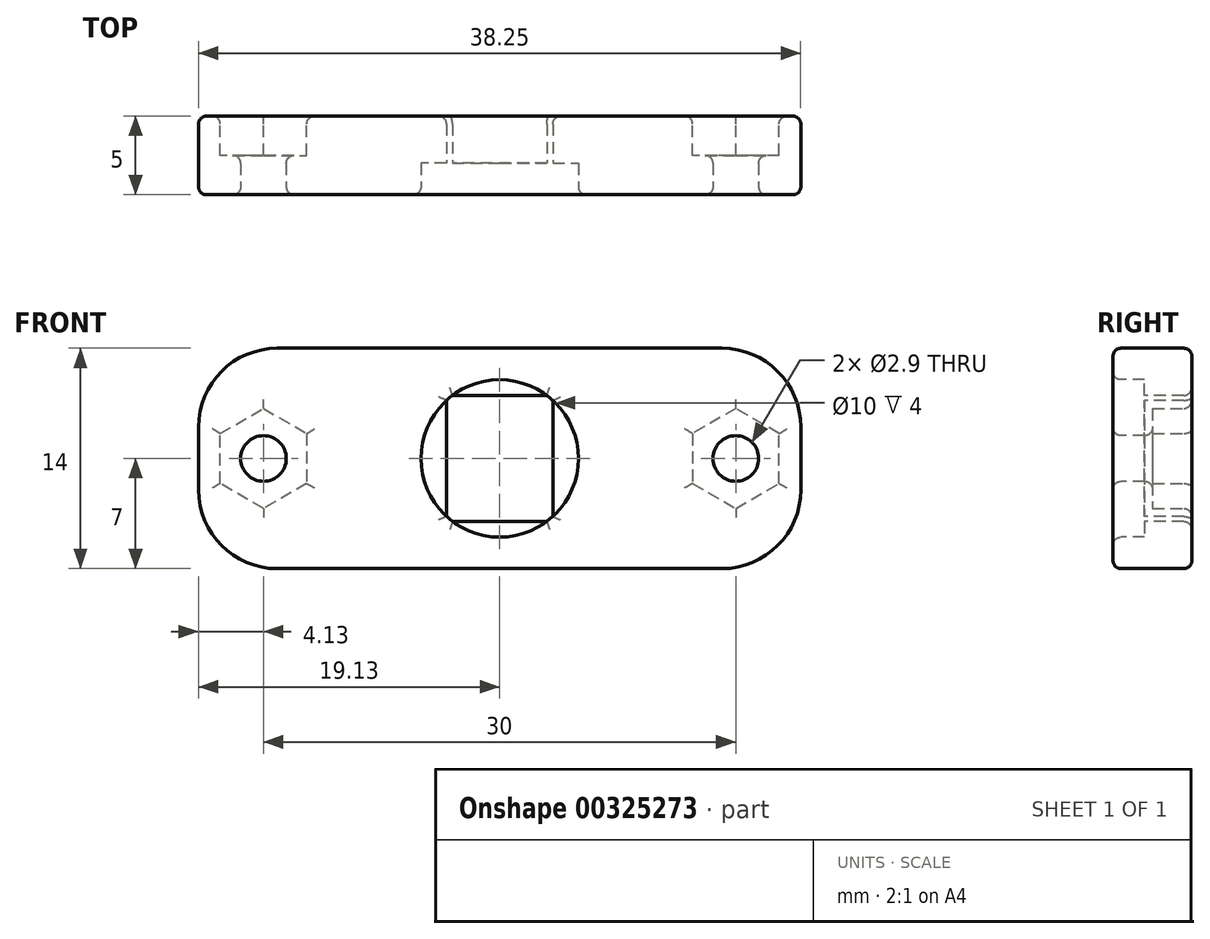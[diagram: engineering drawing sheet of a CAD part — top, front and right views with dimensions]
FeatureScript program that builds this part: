
annotation { "Feature Type Name" : "Feature", "Feature Type Description" : "" }
export const myFeature = defineFeature(function(context is Context, id is Id, definition is map)
    precondition{}
    {
        {
            var Q0;
            Q0=qCreatedBy(makeId("Front.planeOp"),FACE);
            var sketch = newSketch(context, id + "F0", { "sketchPlane" : qUnion([Q0])});
            skLineSegment(sketch, "E0.bottom", {"start": v(14.12, 7) * mm, "end": v(-14.12, 7) * mm});
            skLineSegment(sketch, "E0.top", {"start": v(14.13, -7) * mm, "end": v(-14.12, -7) * mm});
            skLineSegment(sketch, "E0.left", {"start": v(19.13, 2) * mm, "end": v(19.13, -2) * mm});
            skLineSegment(sketch, "E0.right", {"start": v(-19.12, 2) * mm, "end": v(-19.12, -2) * mm});
            skPoint(sketch, "E1.visualSharp", {"position": v(19.13, 7) * mm});
            skArc(sketch, "E1.filletArc", {"start": v(19.13, 2) * mm, "mid": v(17.66, 5.54) * mm, "end": v(14.12, 7) * mm});
            skPoint(sketch, "E2.visualSharp", {"position": v(19.13, -7) * mm});
            skArc(sketch, "E2.filletArc", {"start": v(14.13, -7) * mm, "mid": v(17.66, -5.54) * mm, "end": v(19.13, -2) * mm});
            skPoint(sketch, "E3.visualSharp", {"position": v(-19.12, -7) * mm});
            skArc(sketch, "E3.filletArc", {"start": v(-19.12, -2) * mm, "mid": v(-17.66, -5.54) * mm, "end": v(-14.12, -7) * mm});
            skPoint(sketch, "E4.visualSharp", {"position": v(-19.12, 7) * mm});
            skArc(sketch, "E4.filletArc", {"start": v(-14.12, 7) * mm, "mid": v(-17.66, 5.54) * mm, "end": v(-19.12, 2) * mm});
            skLineSegment(sketch, "E5", {"start": v(19.13, 0) * mm, "end": v(-19.12, 0) * mm, "construction": true});
            skCircle(sketch, "E6", {"center": v(-15, 0) * mm, "radius": 1.45 * mm});
            skCircle(sketch, "E7.MirrorC", {"center": v(15, 0) * mm, "radius": 1.45 * mm});
            skPoint(sketch, "E8", {"position": v(0, 0) * mm});
            skSolve(sketch);
        }
        {
            var Q0;
            Q0 = qSketchRegion(id + "F0", true);
            extrude(context, id + "F1", {"entities" : qUnion([Q0]), "oppositeDirection" : true, "depth" : 5 * mm});
        }
        {
            var Q0;
            Q0=makeQuery(id+"F1.opExtrude","CAP_FACE",FACE,{"disambiguationData":[OSD([sQuery(id+"F0.wireOp",EDGE,"E0.bottom"),sQuery(id+"F0.wireOp",EDGE,"E0.top"),sQuery(id+"F0.wireOp",EDGE,"E0.left"),sQuery(id+"F0.wireOp",EDGE,"E0.right"),sQuery(id+"F0.wireOp",EDGE,"E1.filletArc"),sQuery(id+"F0.wireOp",EDGE,"E2.filletArc"),sQuery(id+"F0.wireOp",EDGE,"E3.filletArc"),sQuery(id+"F0.wireOp",EDGE,"E4.filletArc"),sQuery(id+"F0.wireOp",EDGE,"E6"),sQuery(id+"F0.wireOp",EDGE,"E7.MirrorC")])],"isStart":false});
            var sketch = newSketch(context, id + "F2", { "sketchPlane" : qUnion([Q0])});
            skCircle(sketch, "E9.cCircle", {"center": v(-15, 0) * mm, "radius": 2.75 * mm, "construction": true});
            skLineSegment(sketch, "E9.0", {"start": v(-12.25, 1.59) * mm, "end": v(-12.25, -1.59) * mm});
            skLineSegment(sketch, "E9.1", {"start": v(-12.25, -1.59) * mm, "end": v(-15, -3.18) * mm});
            skLineSegment(sketch, "E9.2", {"start": v(-15, -3.18) * mm, "end": v(-17.75, -1.59) * mm});
            skLineSegment(sketch, "E9.3", {"start": v(-17.75, -1.59) * mm, "end": v(-17.75, 1.59) * mm});
            skLineSegment(sketch, "E9.4", {"start": v(-17.75, 1.59) * mm, "end": v(-15, 3.18) * mm});
            skLineSegment(sketch, "E9.5", {"start": v(-15, 3.18) * mm, "end": v(-12.25, 1.59) * mm});
            skPoint(sketch, "E9.0.midPoint", {"position": v(-12.25, 0) * mm});
            skLineSegment(sketch, "E10.MirrorCS", {"start": v(15, 3.18) * mm, "end": v(12.25, 1.59) * mm});
            skLineSegment(sketch, "E11.MirrorCS", {"start": v(12.25, -1.59) * mm, "end": v(15, -3.18) * mm});
            skLineSegment(sketch, "E12.MirrorCS", {"start": v(12.25, 1.59) * mm, "end": v(12.25, -1.59) * mm});
            skLineSegment(sketch, "E13.MirrorCS", {"start": v(17.75, 1.59) * mm, "end": v(15, 3.18) * mm});
            skLineSegment(sketch, "E14.MirrorCS", {"start": v(17.75, -1.59) * mm, "end": v(17.75, 1.59) * mm});
            skPoint(sketch, "E15.MirrorP", {"position": v(12.25, 0) * mm});
            skCircle(sketch, "E16.MirrorC", {"center": v(15, 0) * mm, "radius": 2.75 * mm, "construction": true});
            skLineSegment(sketch, "E17.MirrorCS", {"start": v(15, -3.18) * mm, "end": v(17.75, -1.59) * mm});
            skSolve(sketch);
        }
        {
            var Q0;
            Q0=makeQuery(id+"F2.imprint","IMPRINT",FACE,{"disambiguationData":[TD([[makeQuery(id+"F2.imprint","IMPRINT",EDGE,{"derivedFrom":sQuery(id+"F2.wireOp",EDGE,"E9.0")}),-1.0]])]});
            var Q1;
            Q1=makeQuery(id+"F2.imprint","IMPRINT",FACE,{"disambiguationData":[TD([[makeQuery(id+"F2.imprint","IMPRINT",EDGE,{"derivedFrom":sQuery(id+"F2.wireOp",EDGE,"E11.MirrorCS")}),1.0]])]});
            extrude(context, id + "F3", {"entities" : qUnion([Q0, Q1]), "operationType" : NewBodyOperationType.REMOVE, "oppositeDirection" : true, "depth" : 2.5 * mm});
        }
        {
            var Q0;
            Q0=qCreatedBy(makeId("Front.planeOp"),FACE);
            var sketch = newSketch(context, id + "F4", { "sketchPlane" : qUnion([Q0])});
            skPoint(sketch, "E18.middle", {"position": v(0, 0) * mm});
            skLineSegment(sketch, "E19.bottom", {"start": v(3, 4) * mm, "end": v(-3, 4) * mm});
            skLineSegment(sketch, "E19.top", {"start": v(3, -4) * mm, "end": v(-3, -4) * mm});
            skLineSegment(sketch, "E19.left", {"start": v(3.37, 3.69) * mm, "end": v(3.37, -3.69) * mm});
            skLineSegment(sketch, "E19.right", {"start": v(-3.38, 3.69) * mm, "end": v(-3.37, -3.69) * mm});
            skCircle(sketch, "E20", {"center": v(0, 0) * mm, "radius": 5 * mm});
            skPoint(sketch, "E21.orphan", {"position": v(-3.38, 4) * mm});
            skPoint(sketch, "E22.orphan", {"position": v(3.37, 4) * mm});
            skPoint(sketch, "E23.orphan", {"position": v(3.37, -4) * mm});
            skPoint(sketch, "E24.orphan", {"position": v(-3.37, -4) * mm});
            skSolve(sketch);
        }
        {
            var Q0;
            Q0 = qSketchRegion(id + "F4", true);
            extrude(context, id + "F5", {"entities" : qUnion([Q0]), "operationType" : NewBodyOperationType.REMOVE, "oppositeDirection" : true, "depth" : 2 * mm});
        }
        {
            var Q0;
            {var subQ3=sQuery(id+"F4.wireOp",EDGE,"E19.bottom");Q0=makeQuery(id+"F4.imprint","IMPRINT",FACE,{"disambiguationData":[TD([[makeQuery(id+"F4.imprint","IMPRINT",EDGE,{"derivedFrom":subQ3}),1.0]])]});}
            extrude(context, id + "F6", {"entities" : qUnion([Q0]), "operationType" : NewBodyOperationType.REMOVE, "endBound" : BoundingType.THROUGH_ALL, "oppositeDirection" : true, "depth" : 25 * mm});
        }
        {
            var Q0;
            Q0=makeQuery(id+"F1.opExtrude","CAP_EDGE",EDGE,{"disambiguationData":[OSD([sQuery(id+"F0.wireOp",EDGE,"E0.bottom")])],"isStart":true});
            var Q1;
            Q1=makeQuery(id+"F1.opExtrude","CAP_EDGE",EDGE,{"disambiguationData":[OSD([sQuery(id+"F0.wireOp",EDGE,"E0.bottom")])],"isStart":false});
            var Q2;
            Q2=makeQuery(id+"F1.opExtrude","CAP_FACE",FACE,{"disambiguationData":[OSD([sQuery(id+"F0.wireOp",EDGE,"E0.bottom"),sQuery(id+"F0.wireOp",EDGE,"E0.top"),sQuery(id+"F0.wireOp",EDGE,"E0.left"),sQuery(id+"F0.wireOp",EDGE,"E0.right"),sQuery(id+"F0.wireOp",EDGE,"E1.filletArc"),sQuery(id+"F0.wireOp",EDGE,"E2.filletArc"),sQuery(id+"F0.wireOp",EDGE,"E3.filletArc"),sQuery(id+"F0.wireOp",EDGE,"E4.filletArc"),sQuery(id+"F0.wireOp",EDGE,"E6"),sQuery(id+"F0.wireOp",EDGE,"E7.MirrorC")])],"isStart":false});
            var Q3;
            Q3=makeQuery(id+"F1.opExtrude","SWEPT_FACE",FACE,{"disambiguationData":[OSD([sQuery(id+"F0.wireOp",EDGE,"E6")])]});
            var Q4;
            Q4=makeQuery(id+"F1.opExtrude","SWEPT_FACE",FACE,{"disambiguationData":[OSD([sQuery(id+"F0.wireOp",EDGE,"E7.MirrorC")])]});
            var Q5;
            Q5=makeQuery(id+"F1.opExtrude","CAP_FACE",FACE,{"disambiguationData":[OSD([sQuery(id+"F0.wireOp",EDGE,"E0.bottom"),sQuery(id+"F0.wireOp",EDGE,"E0.top"),sQuery(id+"F0.wireOp",EDGE,"E0.left"),sQuery(id+"F0.wireOp",EDGE,"E0.right"),sQuery(id+"F0.wireOp",EDGE,"E1.filletArc"),sQuery(id+"F0.wireOp",EDGE,"E2.filletArc"),sQuery(id+"F0.wireOp",EDGE,"E3.filletArc"),sQuery(id+"F0.wireOp",EDGE,"E4.filletArc"),sQuery(id+"F0.wireOp",EDGE,"E6"),sQuery(id+"F0.wireOp",EDGE,"E7.MirrorC")])],"isStart":true});
            fillet(context, id + "F7", {"entities" : qUnion([Q0, Q1, Q2, Q3, Q4, Q5]), "radius" : .5 * mm, "tangentPropagation" : true, "allowEdgeOverflow" : false});
        }
    });
